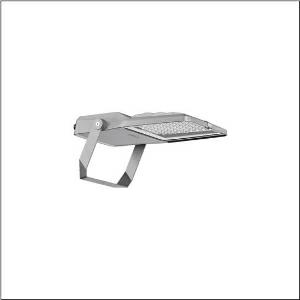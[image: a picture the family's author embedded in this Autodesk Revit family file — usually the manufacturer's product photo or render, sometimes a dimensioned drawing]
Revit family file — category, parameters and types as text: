
# Revit family: floodlight_fl_21_iq_mini___pl52_5xa7772d1d1a_9c36
name_source: partatom
category: Lighting Fixtures
units: mm (PartAtom-declared; Revit-internal decimal feet)

## family parameters
Cut with Voids When Loaded = No
Host = Face
Light Source = No
Part Type = Normal
Room Calculation Point = No
Round Connector Dimension = Use Diameter
Shared = No

## types (1)
- --- (1 x LED, 14760 lm, 143 W, 2200K)
    Apparent Load = 143 VA
    CIE Flux Codes = 26 60 98 100 100
    Color Rendering = 70
    Color Temperature = 2200K
    Default Elevation = 1800 mm
    Description = Floodlight FL 21 iQ mini, floodlight, primary light control with lens, of PMMA, primary optical cover: protective disc, of toughened safety glass, transparent, light distribution: PL52, light emission: direct distribution, installation type: surface-mounted, LED, High Power LED, rated luminous flux: 14.760lm, luminous efficacy: 103lm/W, light colour: 722, colour temperature: 2200K, control gear: iQ Street-Remote/DALI, control: Street-Remote, Auto-Match, Temp-Guard, Night-Set, Smart-Wire, Desk-Remote (wireless, voltage-free reading and setting of iQ features in the workshop via application-optimized NFC function/RFID function), optimised constant luminous flux control (CLO 2.0), with terminal, 6-pole, mains connection: 220..240V, AC, 50/60Hz, start of lifetime: 143W, end of service life: 152W, reduction: 61W, luminaire housing, of diecast aluminium, powder-coated, Siteco® metallic grey (DB 702S), corrosivity category C5 mid according to DIN EN ISO 12944, suitable for swimming pools, chlorine-resistant, sealing non-destructively replaceable, mounting bracket, of steel, galvanised, powder-coated, Siteco® metallic grey (DB 702S), protection rating (complete): IP66, insulation class (complete): insulation class II (safety insulation), certification: CE, ENEC, VDE, protection symbol: D, impact resistance: IK08, permissible operating ambient temperature: -40..+40°C, permissible operating ambient temperature for outdoor applications: -40..+50°C, standard: DIN EN 12944, LABS conformity tested according to VDMA 24364:2018-05, packaging unit: 1 piece

Light Distribution: PL52
    Height = 70 mm
    Lamp = 1 x LED
    Lamp Light Flux = 14760 lm
    Lamp Power = 143 W
    Lamp count = 1
    Length = 485 mm
    Luminous efficacy = 103 lm/W
    Manufacturer = Siteco
    ModVariant = No
    Model = 5XA7772D1D1A
    Number of Poles = 1
    OnlyDefault = Yes
    Power Factor = 1
    Product Name = Floodlight FL 21 iQ mini | PL52
    Product group = floodlight | pylon annexe
    ProductGroupID = 6200
    Protection Class = Protection class II
    Protection Degree = IP 66
    RLX_Detail_Level = 1
    RLX_Emergency_Light_Flux = 0 lm
    RLX_Emergency_Type = 0
    RLX_Emergency_Type_DB = No
    RlxData = <blob elided: 96705 chars, md5=2964d0b8>
    Socket = socket
    Standby Power = 0 W
    System Light Flux = 14760 lm
    System Power = 143 W
    Type Comments = factory setting: luminous flux: 100 % | dim-lin: 254 | 730 mA
    Type Image = l_1006845.jpg
    URL = http://relux.com
    VarID = @adj_163826
    Voltage = 0 V
    Weight = 0.00 kg
    Width = 337 mm

## geometry (parser evidence)
native form markers: Blend x4, Sweep x12
no freeform markers — native parametric forms only
